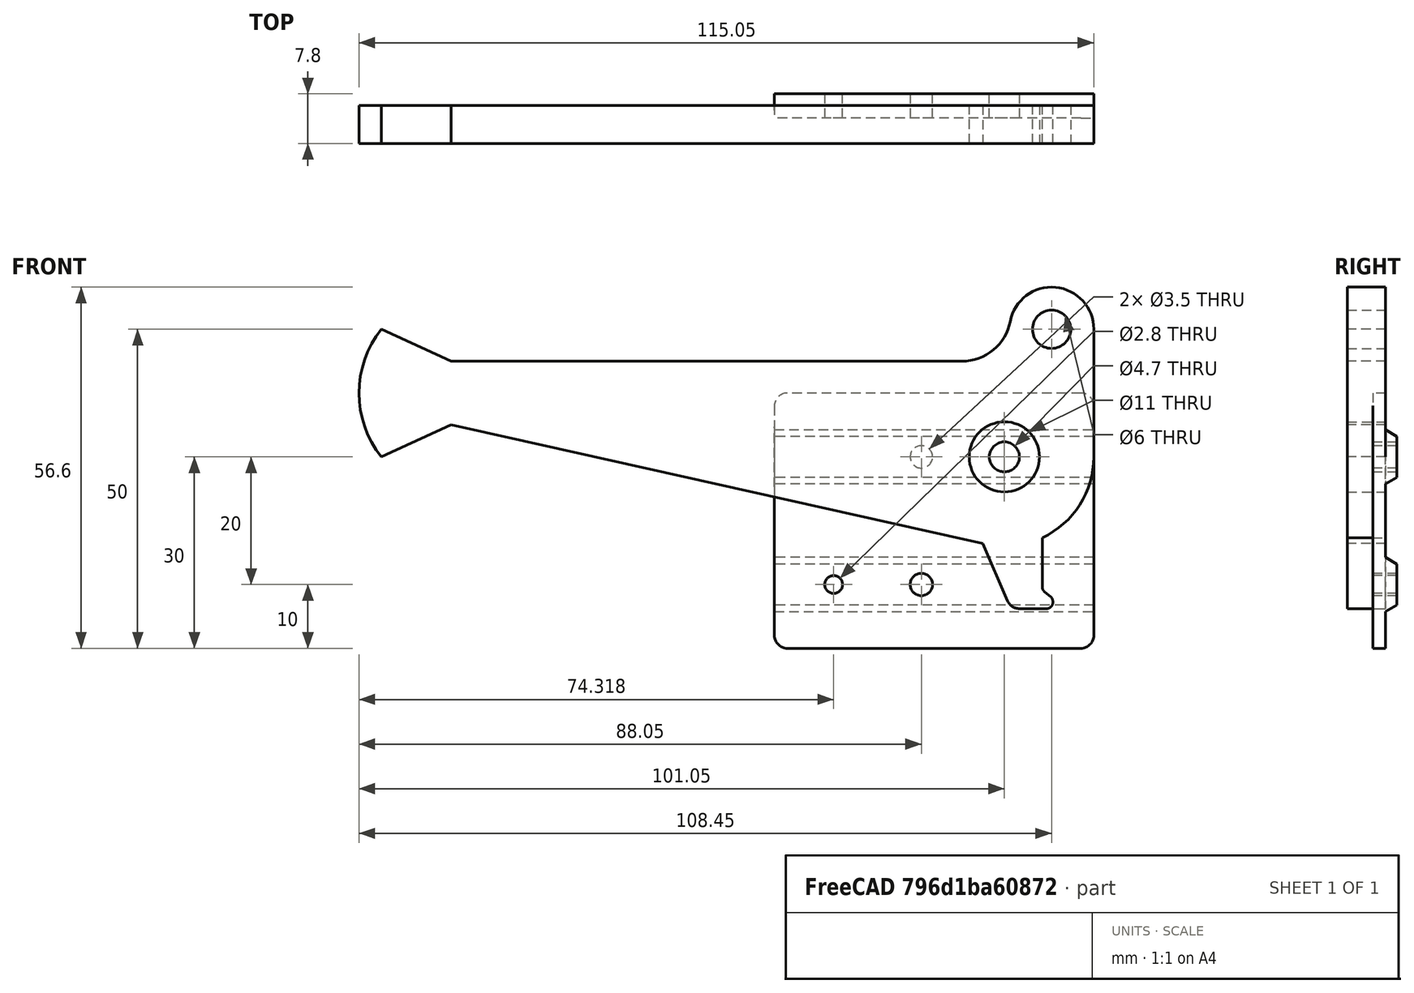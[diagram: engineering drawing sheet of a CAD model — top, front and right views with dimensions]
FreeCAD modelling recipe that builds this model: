
FCSTD DOCUMENT  (FreeCAD 0.19R)
Label: PointerBody
License: All rights reserved
LicenseURL: http://en.wikipedia.org/wiki/All_rights_reserved
objects: Sketcher::SketchObject×9, PartDesign::Fillet×8, PartDesign::Pad×4, PartDesign::Body×2, PartDesign::Pocket×2, Mesh::Feature×2
note: 39 computed .brp shape members not serialized (recipe doc carries the construction recipe); baked Part::Feature solids carry a one-line shape summary decoded from their .brp

FEATURE [Sketcher::SketchObject] Sketch
  FullyConstrained = true
  MapMode = 5
  Placement = pos=(0,0,0) rot=(1,0,0;1.5708rad)
  Support = -> [XZ_Plane]
  sketch-geometry (20):
    g0: LineSegment StartX=-150 StartY=0 StartZ=0 EndX=150 EndY=0 EndZ=0
    g1: LineSegment StartX=150 StartY=0 StartZ=0 EndX=150 EndY=-60 EndZ=0
    g2: LineSegment StartX=150 StartY=-60 StartZ=0 EndX=-150 EndY=-60 EndZ=0
    g3: LineSegment StartX=-150 StartY=-60 StartZ=0 EndX=-150 EndY=0 EndZ=0
    g4: LineSegment StartX=100 StartY=90.56 StartZ=0 EndX=140 EndY=90.56 EndZ=0
    g5: LineSegment StartX=140 StartY=90.56 StartZ=0 EndX=140 EndY=-159.1 EndZ=0
    g6: LineSegment StartX=140 StartY=-159.1 StartZ=0 EndX=100 EndY=-159.1 EndZ=0
    g7: LineSegment StartX=100 StartY=-159.1 StartZ=0 EndX=100 EndY=90.56 EndZ=0
    g8: LineSegment StartX=-197.14 StartY=-10 StartZ=0 EndX=297.12 EndY=-10 EndZ=0
    g9: Circle CenterX=92.4 CenterY=10 CenterZ=0 NormalX=0 NormalY=0 NormalZ=1 AngleXU=0 Radius=3
    g10: Circle CenterX=85 CenterY=-10 CenterZ=0 NormalX=0 NormalY=0 NormalZ=1 AngleXU=0 Radius=5.5
    g11: ArcOfCircle CenterX=0 CenterY=0 CenterZ=0 NormalX=0 NormalY=0 NormalZ=1 AngleXU=0 Radius=16.0459 StartAngle=2.46875 EndAngle=3.81444
    g12: LineSegment StartX=78.36 StartY=5 StartZ=0 EndX=-1.64 EndY=5 EndZ=0
    g13: LineSegment StartX=-1.64 StartY=5 StartZ=0 EndX=-12.5487 EndY=10 EndZ=0
    g14: LineSegment StartX=81.9492 StartY=-23.6636 StartZ=0 EndX=-1.64 EndY=-5 EndZ=0
    g15: LineSegment StartX=-1.64 StartY=-5 StartZ=0 EndX=-12.5487 EndY=-10 EndZ=0
    g16: ArcOfCircle CenterX=85 CenterY=-10 CenterZ=0 NormalX=0 NormalY=0 NormalZ=1 AngleXU=0 Radius=14 StartAngle=4.49272 EndAngle=6.28319
    g17: ArcOfCircle CenterX=92.4 CenterY=10 CenterZ=0 NormalX=0 NormalY=0 NormalZ=1 AngleXU=0 Radius=6.6 StartAngle=0 EndAngle=2.95184
    g18: LineSegment StartX=99 StartY=-10 StartZ=0 EndX=99 EndY=10 EndZ=0
    g19: ArcOfCircle CenterX=78.36 CenterY=12.6966 CenterZ=0 NormalX=0 NormalY=0 NormalZ=1 AngleXU=0 Radius=7.69662 StartAngle=4.71239 EndAngle=6.09343
  constraints (55):
    c: Coincident(g0,g1)
    c: Coincident(g1,g2)
    c: Coincident(g2,g3)
    c: Coincident(g3,g0)
    c: Horizontal(g0)
    c: Horizontal(g2)
    c: Vertical(g1)
    c: Vertical(g3)
    c: Symmetric(g0,g0,g-1)
    c: Distance(g0) = 300
    c: Coincident(g4,g5)
    c: Coincident(g5,g6)
    c: Coincident(g6,g7)
    c: Coincident(g7,g4)
    c: Horizontal(g4)
    c: Horizontal(g6)
    c: Vertical(g5)
    c: Vertical(g7)
    c: DistanceX(g-1,g6) = 100
    c: Distance(g4) = 40
    c: Horizontal(g8)
    c: DistanceY(g8) = -10
    c: Distance(g3) = 60
    c: Distance(g8) = 494.26
    c: DistanceX(g8) = -197.14
    c: DistanceY(g6) = -159.1
    c: DistanceY(g4) = 90.56
    c: Diameter(g9) = 6
    c: Distance(g9,g7) = 7.6
    c: DistanceY(g9) = 10
    c: Diameter(g10) = 11
    c: Distance(g10,g7) = 15
    c: Coincident(g11,g-1)
    c: PointOnObject(g10,g8)
    c: Horizontal(g12)
    c: Coincident(g12,g13)
    c: Coincident(g13,g11)
    c: Coincident(g14,g15)
    c: Coincident(g15,g11)
    c: Symmetric(g14,g12,g0)
    c: Distance(g15) = 12
    c: Symmetric(g11,g11,g0)
    c: Distance(g12,g14) = 10
    c: Coincident(g16,g10)
    c: Coincident(g17,g9)
    c: Tangent(g18,g16) = -1.5708
    c: Tangent(g18,g17) = -1.5708
    c: Tangent(g16,g14) = 1.5708
    c: Vertical(g18)
    c: Distance(g17,g7) = 1
    c: Tangent(g19,g17) = 1.5708
    c: Tangent(g12,g19) = 1.5708
    c: Distance(g11,g11) = 20
    c: Distance(g12) = 80
    c: DistanceX(g12) = 78.36
FEATURE [PartDesign::Pad] Pad
  Direction = (1,1,1)
  Length = 6
  Length2 = 100
  Placement = pos=(0,0,0) rot=(1,0,0;1.5708rad)
  Profile = -> Sketch
  Type = 0
FEATURE [Sketcher::SketchObject] Sketch001
  FullyConstrained = false
  MapMode = 5
  Placement = pos=(0,3.3e-15,5) rot=(0,0,1;3.14159rad)
  Support = -> [Pad]
  sketch-geometry (12):
    g0: LineSegment StartX=-140.762 StartY=22.8 StartZ=0 EndX=-100.762 EndY=22.8 EndZ=0
    g1: LineSegment StartX=-100.762 StartY=22.8 StartZ=0 EndX=-100.762 EndY=2.8 EndZ=0
    g2: LineSegment StartX=-100.762 StartY=2.8 StartZ=0 EndX=-140.762 EndY=2.8 EndZ=0
    g3: LineSegment StartX=-140.762 StartY=2.8 StartZ=0 EndX=-140.762 EndY=22.8 EndZ=0
    g4: LineSegment StartX=-96.3839 StartY=12.8385 StartZ=0 EndX=-88.3839 EndY=12.8385 EndZ=0
    g5: LineSegment StartX=-88.3839 StartY=12.8385 StartZ=0 EndX=-88.3839 EndY=6.13849 EndZ=0
    g6: LineSegment StartX=-88.3839 StartY=6.13849 StartZ=0 EndX=-96.3839 EndY=6.13849 EndZ=0
    g7: LineSegment StartX=-96.3839 StartY=6.13849 StartZ=0 EndX=-96.3839 EndY=12.8385 EndZ=0
    g8: LineSegment StartX=-100.762 StartY=21.6385 StartZ=0 EndX=-85.4622 EndY=21.6385 EndZ=0
    g9: LineSegment StartX=-85.4622 StartY=21.6385 StartZ=0 EndX=-85.4622 EndY=12.8385 EndZ=0
    g10: LineSegment StartX=-85.4622 StartY=12.8385 StartZ=0 EndX=-100.762 EndY=12.8385 EndZ=0
    g11: LineSegment StartX=-100.762 StartY=12.8385 StartZ=0 EndX=-100.762 EndY=21.6385 EndZ=0
  constraints (33):
    c: Coincident(g0,g1)
    c: Coincident(g1,g2)
    c: Coincident(g2,g3)
    c: Coincident(g3,g0)
    c: Horizontal(g0)
    c: Horizontal(g2)
    c: Vertical(g1)
    c: Vertical(g3)
    c: DistanceY(g-1,g1) = 2.8
    c: Distance(g1) = 20
    c: Distance(g0) = 40
    c: Coincident(g4,g5)
    c: Coincident(g5,g6)
    c: Coincident(g6,g7)
    c: Coincident(g7,g4)
    c: Horizontal(g4)
    c: Horizontal(g6)
    c: Vertical(g5)
    c: Vertical(g7)
    c: Distance(g5) = 6.7
    c: Distance(g4) = 8
    c: Coincident(g8,g9)
    c: Coincident(g9,g10)
    c: Coincident(g10,g11)
    c: Coincident(g11,g8)
    c: Horizontal(g8)
    c: Horizontal(g10)
    c: Vertical(g9)
    c: Vertical(g11)
    c: Distance(g9) = 8.8
    c: PointOnObject(g4,g10)
    c: Distance(g8) = 15.3
    c: PointOnObject(g8,g1)
FEATURE [Sketcher::SketchObject] Sketch002
  FullyConstrained = true
  MapMode = 5
  Placement = pos=(0,0,0) rot=(1,0,0;1.5708rad)
  Support = -> [XZ_Plane]
FEATURE [Sketcher::SketchObject] Sketch003
  FullyConstrained = true
  MapMode = 5
  Support = -> [XY_Plane]
FEATURE [Sketcher::SketchObject] Sketch004
  FullyConstrained = false
  MapMode = 5
  Placement = pos=(0,-6,2.7e-15) rot=(1,0,0;1.5708rad)
  Support = -> [Pad]
  sketch-geometry (6):
    g0: LineSegment StartX=81.1405 StartY=-22.4473 StartZ=0 EndX=90.934 EndY=-21.5023 EndZ=0
    g1: LineSegment StartX=90.934 StartY=-21.5023 StartZ=0 EndX=90.934 EndY=-30.8664 EndZ=0
    g2: LineSegment StartX=90.934 StartY=-30.8664 StartZ=0 EndX=92.5663 EndY=-32.155 EndZ=0
    g3: LineSegment StartX=92.5663 StartY=-32.155 StartZ=0 EndX=92.6522 EndY=-33.7873 EndZ=0
    g4: LineSegment StartX=92.6522 StartY=-33.7873 StartZ=0 EndX=86.0372 EndY=-33.7873 EndZ=0
    g5: LineSegment StartX=86.0372 StartY=-33.7873 StartZ=0 EndX=81.1405 EndY=-22.4473 EndZ=0
  constraints (8):
    c: Coincident(g0,g1)
    c: Vertical(g1)
    c: Coincident(g1,g2)
    c: Coincident(g2,g3)
    c: Coincident(g3,g4)
    c: Horizontal(g4)
    c: Coincident(g4,g5)
    c: Coincident(g5,g0)
FEATURE [PartDesign::Pad] Pad001
  BaseFeature = -> Pad
  Direction = (1,1,1)
  Length = 6
  Length2 = 100
  Placement = pos=(0,0,0) rot=(1,0,0;1.5708rad)
  Profile = -> Sketch004
  Reversed = true
  Type = 0
FEATURE [PartDesign::Fillet] Fillet
  Base = -> Pad001 [Edge53]
  BaseFeature = -> Pad001
  Placement = pos=(0,0,0) rot=(1,0,0;1.5708rad)
  Radius = 2
  SupportTransform = false
FEATURE [PartDesign::Fillet] Fillet001
  Base = -> Fillet [Edge18]
  BaseFeature = -> Fillet
  Placement = pos=(0,0,0) rot=(1,0,0;1.5708rad)
  Radius = 1
  SupportTransform = false
FEATURE [PartDesign::Fillet] Fillet002
  Base = -> Fillet001 [Edge18]
  BaseFeature = -> Fillet001
  Placement = pos=(0,0,0) rot=(1,0,0;1.5708rad)
  Radius = 1
  SupportTransform = false
FEATURE [PartDesign::Fillet] Fillet003
  Base = -> Fillet002 [Edge19]
  BaseFeature = -> Fillet002
  Placement = pos=(0,0,0) rot=(1,0,0;1.5708rad)
  Radius = 1
  SupportTransform = false
FEATURE [PartDesign::Body] Body  label="Pointer"
  Group = -> [Sketch,Pad,Sketch001,Sketch002,Sketch003,Sketch004,Pad001,Fillet,Fillet001,Fillet002,Fillet003]
  Origin = -> Origin
  Tip = -> Fillet003
FEATURE [Sketcher::SketchObject] Sketch005
  FullyConstrained = true
  MapMode = 5
  Placement = pos=(0,0,0) rot=(1,0,0;1.5708rad)
  Support = -> [XZ_Plane001]
  sketch-geometry (4):
    g0: LineSegment StartX=99 StartY=0 StartZ=0 EndX=49 EndY=0 EndZ=0
    g1: LineSegment StartX=49 StartY=0 StartZ=0 EndX=49 EndY=-40 EndZ=0
    g2: LineSegment StartX=49 StartY=-40 StartZ=0 EndX=99 EndY=-40 EndZ=0
    g3: LineSegment StartX=99 StartY=-40 StartZ=0 EndX=99 EndY=0 EndZ=0
  constraints (12):
    c: Coincident(g0,g1)
    c: Coincident(g1,g2)
    c: Coincident(g2,g3)
    c: Coincident(g3,g0)
    c: Horizontal(g0)
    c: Horizontal(g2)
    c: Vertical(g1)
    c: Vertical(g3)
    c: PointOnObject(g0,g-1)
    c: Distance(g3) = 40
    c: DistanceX(g2) = 99
    c: DistanceX(g1) = 49
FEATURE [PartDesign::Pad] Pad002
  Direction = (1,1,1)
  Length = 2
  Length2 = 100
  Placement = pos=(0,0,0) rot=(1,0,0;1.5708rad)
  Profile = -> Sketch005
  Type = 0
FEATURE [Sketcher::SketchObject] Sketch006
  FullyConstrained = false
  MapMode = 5
  Placement = pos=(99,0,0) rot=(0.707107,0,0.707107;3.14159rad)
  Support = -> [Pad002]
  sketch-geometry (9):
    g0: LineSegment StartX=-34.7 StartY=0.798076 StartZ=0 EndX=-33.2 EndY=-1.8 EndZ=0
    g1: LineSegment StartX=-33.2 StartY=-1.8 StartZ=0 EndX=-26.8 EndY=-1.8 EndZ=0
    g2: LineSegment StartX=-26.8 StartY=-1.8 StartZ=0 EndX=-25.3 EndY=0.798076 EndZ=0
    g3: LineSegment StartX=-5.3 StartY=0.798076 StartZ=0 EndX=-6.8 EndY=-1.8 EndZ=0
    g4: LineSegment StartX=-6.8 StartY=-1.8 StartZ=0 EndX=-13.2 EndY=-1.8 EndZ=0
    g5: LineSegment StartX=-13.2 StartY=-1.8 StartZ=0 EndX=-14.7 EndY=0.798076 EndZ=0
    g6: LineSegment StartX=-10 StartY=4.17761 StartZ=0 EndX=-10 EndY=2.77278 EndZ=0
    g7: LineSegment StartX=-14.7 StartY=0.798076 StartZ=0 EndX=-5.3 EndY=0.798076 EndZ=0
    g8: LineSegment StartX=-34.7 StartY=0.798076 StartZ=0 EndX=-25.3 EndY=0.798076 EndZ=0
  constraints (25):
    c: Coincident(g0,g1)
    c: Horizontal(g1)
    c: Coincident(g1,g2)
    c: Coincident(g3,g4)
    c: Horizontal(g4)
    c: Coincident(g4,g5)
    c: Distance(g4) = 6.4
    c: Distance(g1) = 6.4
    c: DistanceY(g3) = -1.8
    c: DistanceY(g1) = -1.8
    c: Distance(g4,g0) = 20
    c: Symmetric(g3,g4,g6)
    c: DistanceX(g6) = -10
    c: Angle(g0) = -1.0472
    c: Angle(g2) = 1.0472
    c: Angle(g5) = 2.0944
    c: Angle(g3) = -2.0944
    c: Coincident(g5,g7)
    c: Coincident(g7,g3)
    c: Horizontal(g7)
    c: Coincident(g8,g0)
    c: Coincident(g8,g2)
    c: Horizontal(g8)
    c: Distance(g5) = 3
    c: Distance(g2) = 3
FEATURE [PartDesign::Pad] Pad003
  BaseFeature = -> Pad002
  Direction = (1,1,1)
  Length = 50
  Length2 = 100
  Placement = pos=(0,0,0) rot=(1,0,0;1.5708rad)
  Profile = -> Sketch006
  Reversed = true
  Type = 0
FEATURE [Sketcher::SketchObject] Sketch007
  FullyConstrained = false
  MapMode = 5
  Placement = pos=(0,0,0) rot=(-1,0,0;1.5708rad)
  Support = -> [Pad003]
  sketch-geometry (1):
    g0: Circle CenterX=85 CenterY=10 CenterZ=0 NormalX=0 NormalY=0 NormalZ=1 AngleXU=0 Radius=2.35
  constraints (2):
    c: Diameter(g0) = 4.7
    c: DistanceY(g0) = 10
FEATURE [PartDesign::Pocket] Pocket
  BaseFeature = -> Pad003
  Length = 15
  Length2 = 100
  Placement = pos=(0,0,0) rot=(1,0,0;1.5708rad)
  Profile = -> Sketch007
  Type = 4
FEATURE [Sketcher::SketchObject] Sketch008
  FullyConstrained = false
  MapMode = 5
  Placement = pos=(0,-2,-4e-16) rot=(1,0,0;1.5708rad)
  Support = -> [Pocket]
  sketch-geometry (3):
    g0: Circle CenterX=58.2681 CenterY=-30 CenterZ=0 NormalX=0 NormalY=0 NormalZ=1 AngleXU=0 Radius=1.4
    g1: Circle CenterX=72 CenterY=-30 CenterZ=0 NormalX=0 NormalY=0 NormalZ=1 AngleXU=0 Radius=1.75
    g2: Circle CenterX=72 CenterY=-10 CenterZ=0 NormalX=0 NormalY=0 NormalZ=1 AngleXU=0 Radius=1.75
  constraints (8):
    c: DistanceY(g0) = -30
    c: Diameter(g0) = 2.8
    c: Diameter(g1) = 3.5
    c: Diameter(g2) = 3.5
    c: DistanceY(g2) = -10
    c: DistanceY(g1) = -30
    c: DistanceX(g2) = 72
    c: DistanceX(g1) = 72
FEATURE [PartDesign::Pocket] Pocket001
  BaseFeature = -> Pocket
  Length = 5
  Length2 = 100
  Placement = pos=(0,0,0) rot=(1,0,0;1.5708rad)
  Profile = -> Sketch008
  Type = 0
FEATURE [PartDesign::Fillet] Fillet004
  Base = -> Pocket001 [Edge25]
  BaseFeature = -> Pocket001
  Placement = pos=(0,0,0) rot=(1,0,0;1.5708rad)
  Radius = 2
  SupportTransform = false
FEATURE [PartDesign::Fillet] Fillet005
  Base = -> Fillet004 [Edge35]
  BaseFeature = -> Fillet004
  Placement = pos=(0,0,0) rot=(1,0,0;1.5708rad)
  Radius = 2
  SupportTransform = false
FEATURE [PartDesign::Fillet] Fillet006
  Base = -> Fillet005 [Edge17]
  BaseFeature = -> Fillet005
  Placement = pos=(0,0,0) rot=(1,0,0;1.5708rad)
  Radius = 2
  SupportTransform = false
FEATURE [PartDesign::Fillet] Fillet007
  Base = -> Fillet006 [Edge39]
  BaseFeature = -> Fillet006
  Placement = pos=(0,0,0) rot=(1,0,0;1.5708rad)
  Radius = 2
  SupportTransform = false
FEATURE [PartDesign::Body] Body001  label="Mount"
  Group = -> [Sketch005,Pad002,Sketch006,Pad003,Sketch007,Pocket,Sketch008,Pocket001,Fillet004,Fillet005,Fillet006,Fillet007]
  Origin = -> Origin001
  Tip = -> Fillet007
FEATURE [Mesh::Feature] Mesh  label="Pointer (Meshed)"
FEATURE [Mesh::Feature] Mesh001  label="Mount (Meshed)"
